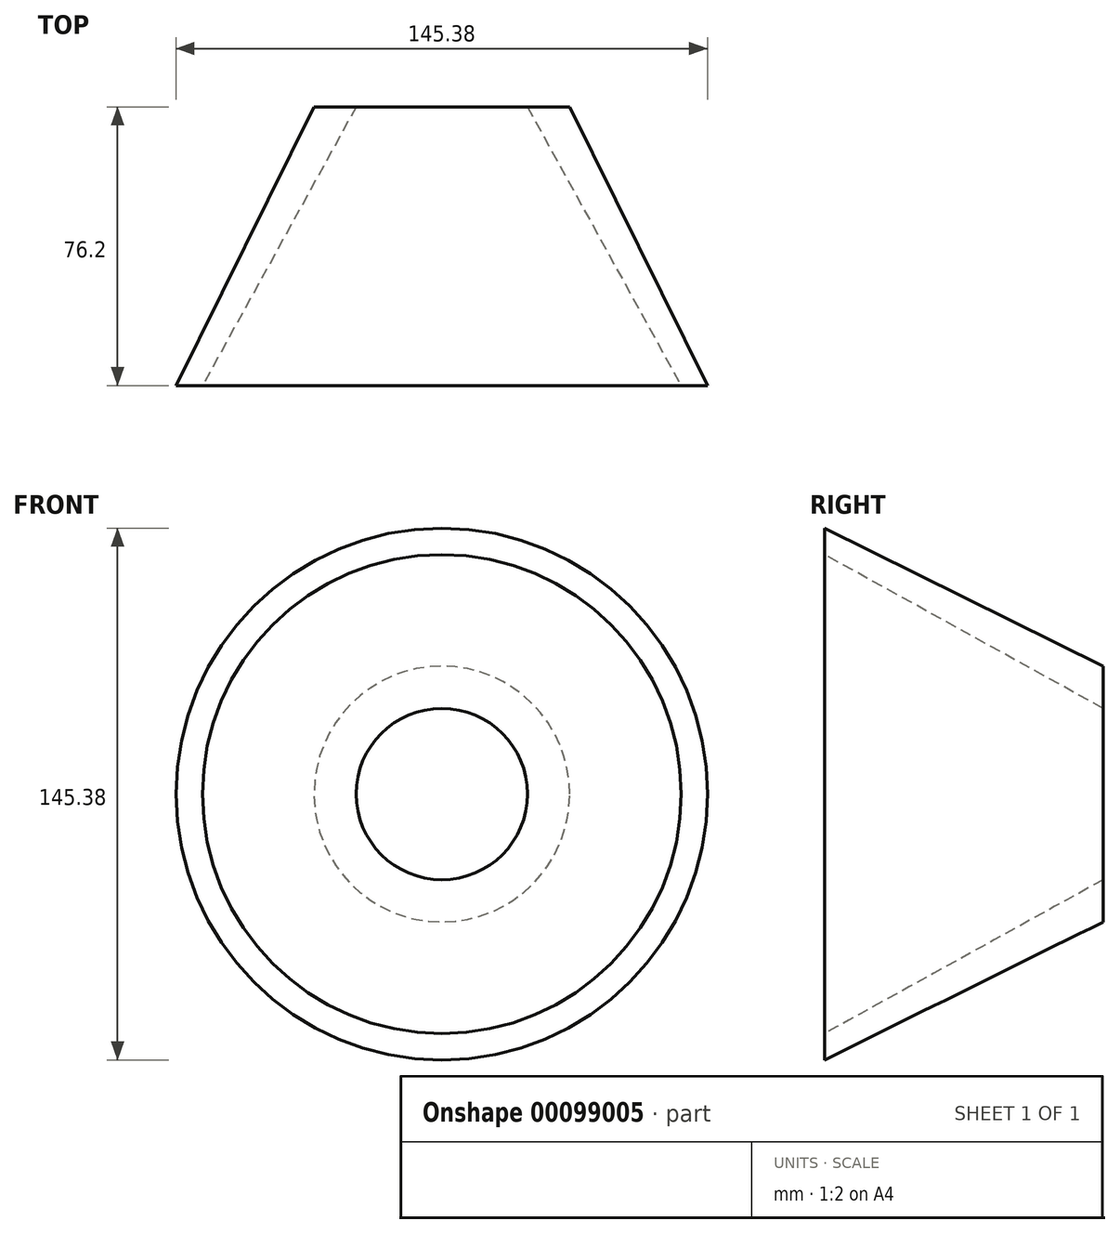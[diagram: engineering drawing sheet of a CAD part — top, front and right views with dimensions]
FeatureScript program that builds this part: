
annotation { "Feature Type Name" : "Feature", "Feature Type Description" : "" }
export const myFeature = defineFeature(function(context is Context, id is Id, definition is map)
    precondition{}
    {
        {
            var Q0;
            Q0=qCreatedBy(makeId("Front.planeOp"),FACE);
            var sketch = newSketch(context, id + "F0", { "sketchPlane" : qUnion([Q0])});
            skCircle(sketch, "E0", {"center": v(0, 0) * mm, "radius": 23.43 * mm, "construction": true});
            skCircle(sketch, "E1", {"center": v(0, 0) * mm, "radius": 34.97 * mm});
            skSolve(sketch);
        }
        {
            var Q0;
            Q0=qCreatedBy(makeId("Front.planeOp"),FACE);
            cPlane(context, id + "F1", {"entities" : qUnion([Q0]), "cplaneType" : CPlaneType.OFFSET, "offset" : 76.2 * mm, "width" : 152.4 * mm, "height" : 152.4 * mm});
        }
        {
            var Q0;
            Q0=qCreatedBy(id+"F1.planeOp",FACE);
            var sketch = newSketch(context, id + "F2", { "sketchPlane" : qUnion([Q0])});
            skCircle(sketch, "E2", {"center": v(0, 0) * mm, "radius": 65.48 * mm, "construction": true});
            skCircle(sketch, "E3", {"center": v(0, 0) * mm, "radius": 72.7 * mm});
            skSolve(sketch);
        }
        {
            var Q0;
            Q0=makeQuery(id+"F2.imprint","IMPRINT",FACE,{"disambiguationData":[TD([[makeQuery(id+"F2.imprint","IMPRINT",EDGE,{"derivedFrom":sQuery(id+"F2.wireOp",EDGE,"E3")}),1.0]])]});
            var Q1;
            Q1=makeQuery(id+"F0.imprint","IMPRINT",FACE,{"disambiguationData":[TD([[makeQuery(id+"F0.imprint","IMPRINT",EDGE,{"derivedFrom":sQuery(id+"F0.wireOp",EDGE,"E1")}),1.0]])]});
            loft(context, id + "F3", {"sheetProfilesArray" : [{ "sheetProfileEntities" : qUnion([Q0]) }, { "sheetProfileEntities" : qUnion([Q1]) }]});
        }
        {
            var Q0;
            Q0=qCreatedBy(id+"F1.planeOp",FACE);
            var sketch = newSketch(context, id + "F4", { "sketchPlane" : qUnion([Q0])});
            skCircle(sketch, "E4.0", {"center": v(0, 0) * mm, "radius": 65.48 * mm});
            skSolve(sketch);
        }
        {
            var Q0;
            Q0=qCreatedBy(makeId("Front.planeOp"),FACE);
            var sketch = newSketch(context, id + "F5", { "sketchPlane" : qUnion([Q0])});
            skCircle(sketch, "E5.0", {"center": v(0, 0) * mm, "radius": 23.43 * mm});
            skSolve(sketch);
        }
        {
            var Q1;
            Q1=makeQuery(id+"F4.imprint","IMPRINT",FACE,{"disambiguationData":[TD([[makeQuery(id+"F4.imprint","IMPRINT",EDGE,{"derivedFrom":sQuery(id+"F4.wireOp",EDGE,"E4.0")}),1.0]])]});
            var Q2;
            Q2=makeQuery(id+"F5.imprint","IMPRINT",FACE,{"disambiguationData":[TD([[makeQuery(id+"F5.imprint","IMPRINT",EDGE,{"derivedFrom":sQuery(id+"F5.wireOp",EDGE,"E5.0")}),1.0]])]});
            loft(context, id + "F6", {"operationType" : NewBodyOperationType.REMOVE, "sheetProfilesArray" : [{ "sheetProfileEntities" : qUnion([Q1]) }, { "sheetProfileEntities" : qUnion([Q2]) }]});
        }
    });
